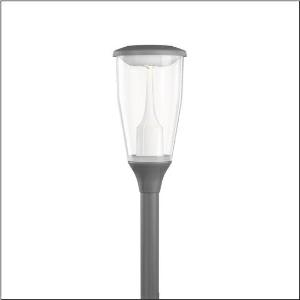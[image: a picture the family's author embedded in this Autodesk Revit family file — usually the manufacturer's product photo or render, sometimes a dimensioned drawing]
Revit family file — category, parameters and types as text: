
# Revit family: dl_11_iq___p1_0a_5xa5575nf14hp00022_d0ce
name_source: partatom
category: Lighting Fixtures
units: mm (PartAtom-declared; Revit-internal decimal feet)

## family parameters
Cut with Voids When Loaded = No
Host = Face
Light Source = No
Part Type = Normal
Room Calculation Point = No
Round Connector Dimension = Use Diameter
Shared = No

## types (1)
- --- (1 x LED, 4280 lm, 33.6 W, 2700K)
    Apparent Load = 34 VA
    CIE Flux Codes = 33 63 91 94 100
    Color Rendering = 70
    Color Temperature = 2700K
    Default Elevation = 1800 mm
    Description = DL 11 iQ, mast luminaire, Module 540 iQ-SR, primary light control with 3 zone facetted reflector, of plastic, silver coated, highly specular, structured, primary optical cover: cover, of PMMA, transparent, light distribution: P1.0a, light emission: direct distribution, primary light characteristic: asymmetric, installation type: post-top, LED, High Power LED, light colour: 727, colour temperature: 2700K, control: Street-Remote, Auto-Match, Temp-Guard, Lumen-Switch, Night-Set, Smart-Wire, Light-Fading, Desk-Remote (wireless, voltage-free reading and setting of iQ features in the workshop via application-optimized NFC function/RFID function), optimised constant luminous flux control (CLO 2.0), mains connection: 220..240V, AC, 50/60Hz, connection cable pre-assembled, cable length: 5,5m, wiring characteristics: H07RN-F, 5-core, 1.5mm², start of lifetime: 34W, end of service life: 36W, luminaire housing, upper part, of diecast aluminium, coated, Siteco® metallic grey (DB 702S), spigot size: 76mm (post-top), post-top mast mounting element, of diecast aluminium, coated, Siteco® metallic grey (DB 702S), Module 540 iQ-SR, traffic white (RAL 9016), equipment: Power, protection rating (complete): IP66, insulation class (complete): insulation class II (safety insulation), certification: CE, ENEC, ENEC+, VDE, packaging unit: 1 piece

Light Distribution: P1.0a
    Height = 665 mm
    Lamp = 1 x LED
    Lamp Light Flux = 4280 lm
    Lamp Power = 33.6 W
    Lamp count = 1
    Length = 334 mm
    Luminous efficacy = 127 lm/W
    Manufacturer = Siteco
    ModVariant = No
    Model = 5XA5575NF14HP00022
    Number of Poles = 1
    OnlyDefault = Yes
    Power Factor = 1
    Product Name = DL 11 iQ | P1.0a
    Product group = mast luminaire | pylon top
    ProductGroupID = 6100
    Protection Class = Protection class II
    Protection Degree = IP 66
    RLX_Detail_Level = 1
    RLX_Emergency_Light_Flux = 0 lm
    RLX_Emergency_Type = 0
    RLX_Emergency_Type_DB = No
    RlxData = <blob elided: 104185 chars, md5=f10c60e8>
    Socket = socket
    Standby Power = 0 W
    System Light Flux = 4280 lm
    System Power = 34 W
    Type Comments = factory setting: luminous flux: 100 % | dim-lin: 254 | 695 mA
    Type Image = l_1258354.jpg
    URL = http://relux.com
    VarID = @adj_001585
    Voltage = 0 V
    Weight = 0.00 kg
    Width = 0 mm  [stored 0 ft]

note: [stored X ft] marks values corroborated as IEEE doubles in the binary element streams (Revit-internal decimal feet)

## geometry (parser evidence)
native form markers: Blend x4, Sweep x9
no freeform markers — native parametric forms only
